# Revit family: Locker-Storage-Foreman-Premium-2_Tier_with_Bench
name_source: partatom
category: Specialty Equipment
units: mm (PartAtom-declared; Revit-internal decimal feet)

## family parameters
Always vertical = Yes
Classification Number = 23.40.20.11.17
Cut with Voids When Loaded = No
Enable Cutting in Views = No
Maintain Annotation Orientation = No
Part Type = Normal
Room Calculation Point = No
Round Connector Dimension = Use Diameter
Shared = No
Work Plane-Based = Yes

## types (1)
- *ERROR* See Type Catalogue
    Bench Offset = 13/16"
    Default Elevation = 48"
    Description = Premium Phenolic Locker with Bench
    Door Height = 19 3/32"
    Keynote = 10 51 00
    Manufacturer = Foreman Lockers
    Model = Phenolic 2-Tier Locker with Bench
    Panel Thickness = 3/8"
    Product Page URL = https://www.arcat.com
    Specification = https://www.arcat.com
    URL = https://foremanlockers.com
    Unit Depth = 18"
    Unit Height = 48"
    Unit Width = 15"

## geometry (parser evidence)
native form markers: Sweep x3
no freeform markers — native parametric forms only
